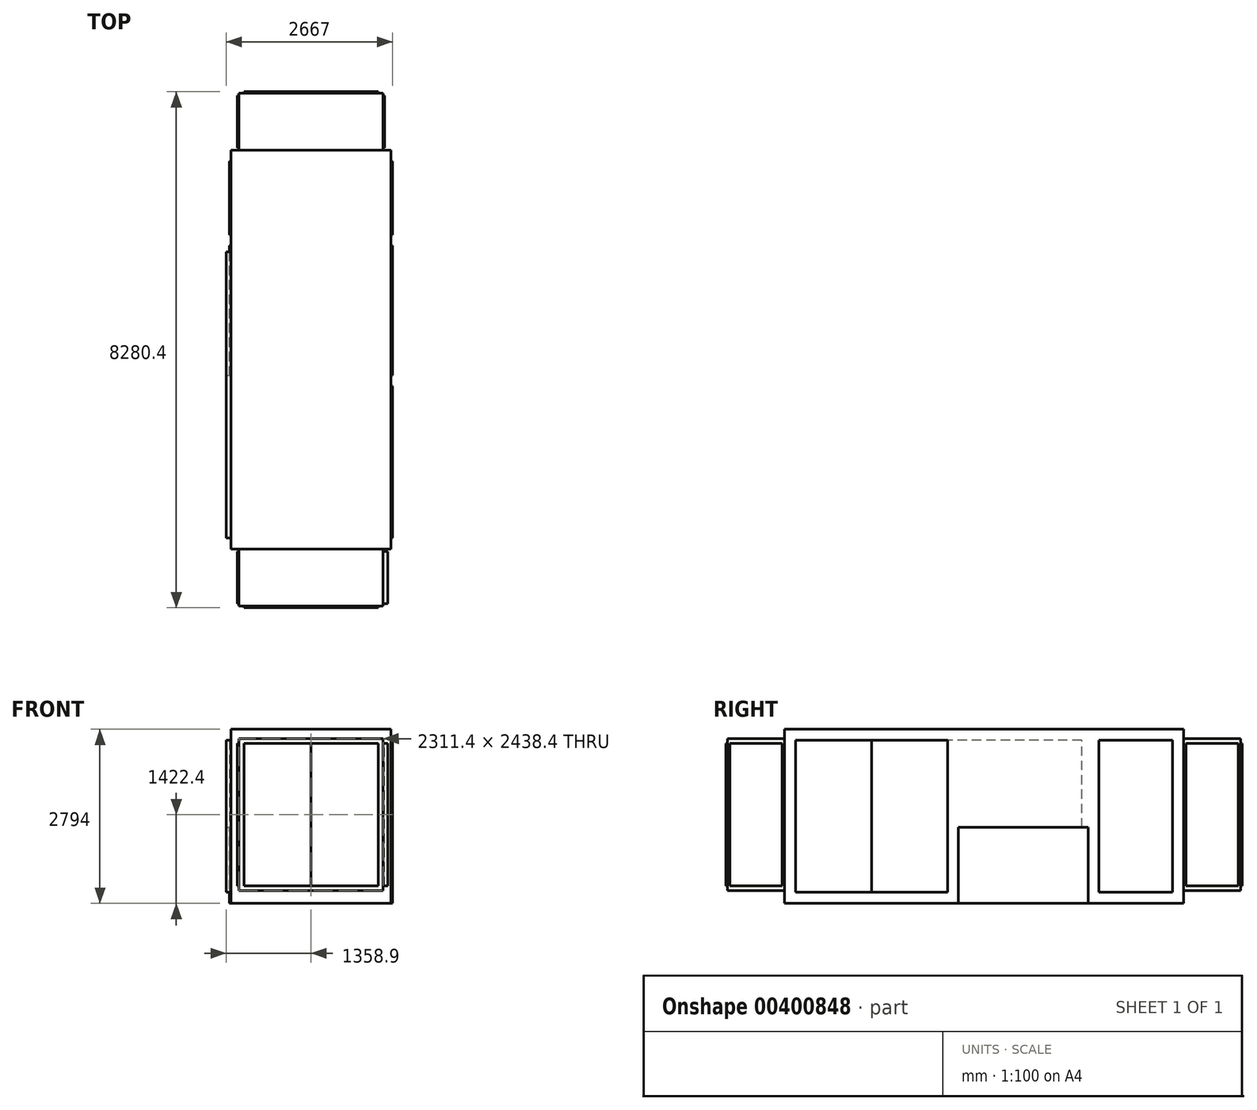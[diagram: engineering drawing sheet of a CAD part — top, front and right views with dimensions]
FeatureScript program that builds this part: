
annotation { "Feature Type Name" : "Feature", "Feature Type Description" : "" }
export const myFeature = defineFeature(function(context is Context, id is Id, definition is map)
    precondition{}
    {
        {
            var Q0;
            Q0=qCreatedBy(makeId("Top.planeOp"),FACE);
            var sketch = newSketch(context, id + "F0", { "sketchPlane" : qUnion([Q0])});
            skLineSegment(sketch, "E0.bottom", {"start": v(0, 0) * mm, "end": v(2565.4, 0) * mm});
            skLineSegment(sketch, "E0.top", {"start": v(0, 6400.8) * mm, "end": v(2565.4, 6400.8) * mm});
            skLineSegment(sketch, "E0.left", {"start": v(0, 0) * mm, "end": v(0, 6400.8) * mm});
            skLineSegment(sketch, "E0.right", {"start": v(2565.4, 0) * mm, "end": v(2565.4, 6400.8) * mm});
            skSolve(sketch);
        }
        {
            var Q0;
            Q0=qSketchRegion(id+"F0",true);
            extrude(context, id + "F1", {"entities" : qUnion([Q0]), "depth" : 2794 * mm});
        }
        {
            var Q0;
            Q0=makeQuery(id+"F1.opExtrude","SWEPT_FACE",FACE,{"disambiguationData":[OSD([sQuery(id+"F0.wireOp",EDGE,"E0.bottom")])]});
            var sketch = newSketch(context, id + "F2", { "sketchPlane" : qUnion([Q0])});
            skLineSegment(sketch, "E1.bottom", {"start": v(127, 203.2) * mm, "end": v(2438.4, 203.2) * mm});
            skLineSegment(sketch, "E1.top", {"start": v(127, 2641.6) * mm, "end": v(2438.4, 2641.6) * mm});
            skLineSegment(sketch, "E1.left", {"start": v(127, 203.2) * mm, "end": v(127, 2641.6) * mm});
            skLineSegment(sketch, "E1.right", {"start": v(2438.4, 203.2) * mm, "end": v(2438.4, 2641.6) * mm});
            skSolve(sketch);
        }
        {
            var Q0;
            Q0=qSketchRegion(id+"F2",true);
            extrude(context, id + "F3", {"entities" : qUnion([Q0]), "operationType" : NewBodyOperationType.ADD, "depth" : 914.4 * mm, "hasSecondDirection" : true, "secondDirectionOppositeDirection" : true, "secondDirectionDepth" : 7315.2 * mm});
        }
        {
            var Q0;
            Q0=makeQuery(id+"F3.opExtrude","CAP_FACE",FACE,{"disambiguationData":[OSD([sQuery(id+"F2.wireOp",EDGE,"E1.bottom"),sQuery(id+"F2.wireOp",EDGE,"E1.top"),sQuery(id+"F2.wireOp",EDGE,"E1.left"),sQuery(id+"F2.wireOp",EDGE,"E1.right")])],"isStart":false});
            var sketch = newSketch(context, id + "F4", { "sketchPlane" : qUnion([Q0])});
            skLineSegment(sketch, "E2.bottom", {"start": v(206.38, 279.4) * mm, "end": v(1282.7, 279.4) * mm});
            skLineSegment(sketch, "E2.top", {"start": v(206.38, 2565.4) * mm, "end": v(1282.7, 2565.4) * mm});
            skLineSegment(sketch, "E2.left", {"start": v(206.38, 279.4) * mm, "end": v(206.38, 2565.4) * mm});
            skLineSegment(sketch, "E2.right", {"start": v(1282.7, 279.4) * mm, "end": v(1282.7, 2565.4) * mm});
            skLineSegment(sketch, "E3.bottom", {"start": v(2359.03, 279.4) * mm, "end": v(1282.7, 279.4) * mm});
            skLineSegment(sketch, "E3.top", {"start": v(2359.03, 2565.4) * mm, "end": v(1282.7, 2565.4) * mm});
            skLineSegment(sketch, "E3.left", {"start": v(2359.03, 279.4) * mm, "end": v(2359.03, 2565.4) * mm});
            skPoint(sketch, "E4", {"position": v(1282.7, 203.2) * mm});
            skPoint(sketch, "E5", {"position": v(2359.03, 1422.4) * mm});
            skPoint(sketch, "E6", {"position": v(2438.4, 1422.4) * mm});
            skSolve(sketch);
        }
        {
            var Q0;
            Q0=makeQuery(id+"F3.opExtrude","CAP_FACE",FACE,{"disambiguationData":[OSD([sQuery(id+"F2.wireOp",EDGE,"E1.bottom"),sQuery(id+"F2.wireOp",EDGE,"E1.top"),sQuery(id+"F2.wireOp",EDGE,"E1.left"),sQuery(id+"F2.wireOp",EDGE,"E1.right")])],"isStart":true});
            var sketch = newSketch(context, id + "F5", { "sketchPlane" : qUnion([Q0])});
            skLineSegment(sketch, "E7.bottom", {"start": v(-2359.02, 279.4) * mm, "end": v(-1282.7, 279.4) * mm});
            skLineSegment(sketch, "E7.top", {"start": v(-2359.02, 2565.4) * mm, "end": v(-1282.7, 2565.4) * mm});
            skLineSegment(sketch, "E7.left", {"start": v(-2359.02, 279.4) * mm, "end": v(-2359.02, 2565.4) * mm});
            skLineSegment(sketch, "E7.right", {"start": v(-1282.7, 279.4) * mm, "end": v(-1282.7, 2565.4) * mm});
            skLineSegment(sketch, "E8.bottom", {"start": v(-206.37, 279.4) * mm, "end": v(-1282.7, 279.4) * mm});
            skLineSegment(sketch, "E8.top", {"start": v(-206.37, 2565.4) * mm, "end": v(-1282.7, 2565.4) * mm});
            skLineSegment(sketch, "E8.left", {"start": v(-206.37, 279.4) * mm, "end": v(-206.37, 2565.4) * mm});
            skPoint(sketch, "E9", {"position": v(-1282.7, 203.2) * mm});
            skPoint(sketch, "E10", {"position": v(-206.37, 1422.4) * mm});
            skPoint(sketch, "E11", {"position": v(-127, 1422.4) * mm});
            skSolve(sketch);
        }
        {
            var Q0;
            Q0=makeQuery(id+"F1.opExtrude","SWEPT_FACE",FACE,{"disambiguationData":[OSD([sQuery(id+"F0.wireOp",EDGE,"E0.right")])]});
            var sketch = newSketch(context, id + "F6", { "sketchPlane" : qUnion([Q0])});
            skLineSegment(sketch, "E12.bottom", {"start": v(177.8, 177.8) * mm, "end": v(1397, 177.8) * mm});
            skLineSegment(sketch, "E12.top", {"start": v(177.8, 2616.2) * mm, "end": v(1397, 2616.2) * mm});
            skLineSegment(sketch, "E12.left", {"start": v(177.8, 177.8) * mm, "end": v(177.8, 2616.2) * mm});
            skLineSegment(sketch, "E12.right", {"start": v(1397, 177.8) * mm, "end": v(1397, 2616.2) * mm});
            skLineSegment(sketch, "E13.bottom", {"start": v(1397, 177.8) * mm, "end": v(2616.2, 177.8) * mm});
            skLineSegment(sketch, "E13.top", {"start": v(1397, 2616.2) * mm, "end": v(2616.2, 2616.2) * mm});
            skLineSegment(sketch, "E13.right", {"start": v(2616.2, 177.8) * mm, "end": v(2616.2, 2616.2) * mm});
            skLineSegment(sketch, "E14", {"start": v(0, 1397) * mm, "end": v(177.8, 1397) * mm, "construction": true});
            skLineSegment(sketch, "E15", {"start": v(1397, 2794) * mm, "end": v(1397, 2616.2) * mm, "construction": true});
            skLineSegment(sketch, "E16.bottom", {"start": v(6223, 2616.2) * mm, "end": v(5041.9, 2616.2) * mm});
            skLineSegment(sketch, "E16.top", {"start": v(6223, 177.8) * mm, "end": v(5041.9, 177.8) * mm});
            skLineSegment(sketch, "E16.left", {"start": v(6223, 2616.2) * mm, "end": v(6223, 177.8) * mm});
            skLineSegment(sketch, "E16.right", {"start": v(5041.9, 2616.2) * mm, "end": v(5041.9, 177.8) * mm});
            skLineSegment(sketch, "E17", {"start": v(6223, 1397) * mm, "end": v(6400.8, 1397) * mm, "construction": true});
            skLineSegment(sketch, "E18.bottom", {"start": v(2787.65, 0) * mm, "end": v(4870.45, 0) * mm});
            skLineSegment(sketch, "E18.top", {"start": v(2787.65, 1219.2) * mm, "end": v(4870.45, 1219.2) * mm});
            skLineSegment(sketch, "E18.left", {"start": v(2787.65, 0) * mm, "end": v(2787.65, 1219.2) * mm});
            skLineSegment(sketch, "E18.right", {"start": v(4870.45, 0) * mm, "end": v(4870.45, 1219.2) * mm});
            skPoint(sketch, "E19", {"position": v(3829.05, 1219.2) * mm});
            skLineSegment(sketch, "E20.bottom", {"start": v(2889.25, 1219.2) * mm, "end": v(4768.85, 1219.2) * mm});
            skLineSegment(sketch, "E20.top", {"start": v(2889.25, 2616.2) * mm, "end": v(4768.85, 2616.2) * mm});
            skLineSegment(sketch, "E20.left", {"start": v(2889.25, 1219.2) * mm, "end": v(2889.25, 2616.2) * mm});
            skLineSegment(sketch, "E20.right", {"start": v(4768.85, 1219.2) * mm, "end": v(4768.85, 2616.2) * mm});
            skLineSegment(sketch, "E21", {"start": v(2616.2, 177.8) * mm, "end": v(2787.65, 177.8) * mm, "construction": true});
            skLineSegment(sketch, "E22", {"start": v(5041.9, 177.8) * mm, "end": v(4870.45, 177.8) * mm, "construction": true});
            skSolve(sketch);
        }
        {
            var Q0;
            Q0=makeQuery(id+"F1.opExtrude","SWEPT_FACE",FACE,{"disambiguationData":[OSD([sQuery(id+"F0.wireOp",EDGE,"E0.left")])]});
            var sketch = newSketch(context, id + "F7", { "sketchPlane" : qUnion([Q0])});
            skLineSegment(sketch, "E23.0.0", {"start": v(-5041.9, 177.8) * mm, "end": v(-6223, 177.8) * mm});
            skLineSegment(sketch, "E23.0.1", {"start": v(-6223, 177.8) * mm, "end": v(-6223, 2616.2) * mm});
            skLineSegment(sketch, "E23.0.2", {"start": v(-6223, 2616.2) * mm, "end": v(-5041.9, 2616.2) * mm});
            skLineSegment(sketch, "E23.0.3", {"start": v(-5041.9, 2616.2) * mm, "end": v(-5041.9, 177.8) * mm});
            skLineSegment(sketch, "E23.1.0", {"start": v(-2787.65, 1219.2) * mm, "end": v(-2787.65, 0) * mm});
            skLineSegment(sketch, "E23.1.1", {"start": v(-2787.65, 0) * mm, "end": v(-4870.45, 0) * mm});
            skLineSegment(sketch, "E23.1.2", {"start": v(-4870.45, 0) * mm, "end": v(-4870.45, 1219.2) * mm});
            skLineSegment(sketch, "E24", {"start": v(-4870.45, 1219.2) * mm, "end": v(-2787.65, 1219.2) * mm});
            skSolve(sketch);
        }
        {
            var Q0;
            {var subQ1=sQuery(id+"F2.wireOp",EDGE,"E1.left");Q0=makeQuery(id+"F3.boolean.opBoolean","SPLIT",FACE,{"disambiguationData":[TD([makeQuery(id+"F1.opExtrude","SWEPT_FACE",FACE,{"disambiguationData":[OSD([sQuery(id+"F0.wireOp",EDGE,"E0.top")])]})])],"derivedFrom":makeQuery(id+"F3.opExtrude","SWEPT_FACE",FACE,{"disambiguationData":[OSD([subQ1])]})});}
            var sketch = newSketch(context, id + "F8", { "sketchPlane" : qUnion([Q0])});
            skLineSegment(sketch, "E25.bottom", {"start": v(-7277.1, 279.4) * mm, "end": v(-6438.9, 279.4) * mm});
            skLineSegment(sketch, "E25.top", {"start": v(-7277.1, 2565.4) * mm, "end": v(-6438.9, 2565.4) * mm});
            skLineSegment(sketch, "E25.left", {"start": v(-7277.1, 279.4) * mm, "end": v(-7277.1, 2565.4) * mm});
            skLineSegment(sketch, "E25.right", {"start": v(-6438.9, 279.4) * mm, "end": v(-6438.9, 2565.4) * mm});
            skPoint(sketch, "E26", {"position": v(-6438.9, 1422.4) * mm});
            skPoint(sketch, "E27", {"position": v(-6858, 279.4) * mm});
            skSolve(sketch);
        }
        {
            var Q0;
            {var subQ0=sQuery(id+"F2.wireOp",EDGE,"E1.left");Q0=makeQuery(id+"F3.boolean.opBoolean","SPLIT",FACE,{"disambiguationData":[TD([makeQuery(id+"F1.opExtrude","SWEPT_FACE",FACE,{"disambiguationData":[OSD([sQuery(id+"F0.wireOp",EDGE,"E0.bottom")])]})])],"derivedFrom":makeQuery(id+"F3.opExtrude","SWEPT_FACE",FACE,{"disambiguationData":[OSD([subQ0])]})});}
            var sketch = newSketch(context, id + "F9", { "sketchPlane" : qUnion([Q0])});
            skLineSegment(sketch, "E28.bottom", {"start": v(38.1, 279.4) * mm, "end": v(876.3, 279.4) * mm});
            skLineSegment(sketch, "E28.top", {"start": v(38.1, 2565.4) * mm, "end": v(876.3, 2565.4) * mm});
            skLineSegment(sketch, "E28.left", {"start": v(38.1, 279.4) * mm, "end": v(38.1, 2565.4) * mm});
            skLineSegment(sketch, "E28.right", {"start": v(876.3, 279.4) * mm, "end": v(876.3, 2565.4) * mm});
            skPoint(sketch, "E29", {"position": v(876.3, 1422.4) * mm});
            skPoint(sketch, "E30", {"position": v(457.2, 279.4) * mm});
            skSolve(sketch);
        }
        {
            var Q0;
            {var subQ1=sQuery(id+"F2.wireOp",EDGE,"E1.right");Q0=makeQuery(id+"F3.boolean.opBoolean","SPLIT",FACE,{"disambiguationData":[TD([makeQuery(id+"F1.opExtrude","SWEPT_FACE",FACE,{"disambiguationData":[OSD([sQuery(id+"F0.wireOp",EDGE,"E0.top")])]})])],"derivedFrom":makeQuery(id+"F3.opExtrude","SWEPT_FACE",FACE,{"disambiguationData":[OSD([subQ1])]})});}
            var sketch = newSketch(context, id + "F10", { "sketchPlane" : qUnion([Q0])});
            skLineSegment(sketch, "E31.0.0", {"start": v(6438.9, 2565.4) * mm, "end": v(7277.1, 2565.4) * mm});
            skLineSegment(sketch, "E31.0.1", {"start": v(7277.1, 2565.4) * mm, "end": v(7277.1, 279.4) * mm});
            skLineSegment(sketch, "E31.0.2", {"start": v(7277.1, 279.4) * mm, "end": v(6438.9, 279.4) * mm});
            skLineSegment(sketch, "E31.0.3", {"start": v(6438.9, 279.4) * mm, "end": v(6438.9, 2565.4) * mm});
            skSolve(sketch);
        }
        {
            var Q0;
            Q0=makeQuery(id+"F7.imprint","IMPRINT",FACE,{"disambiguationData":[TD([[makeQuery(id+"F7.imprint","IMPRINT",EDGE,{"derivedFrom":sQuery(id+"F7.wireOp",EDGE,"E23.0.0")}),1.0]])]});
            var sketch = newSketch(context, id + "F11", { "sketchPlane" : qUnion([Q0])});
            skLineSegment(sketch, "E32.bottom", {"start": v(-4768.85, 1219.2) * mm, "end": v(-2787.65, 1219.2) * mm});
            skLineSegment(sketch, "E32.top", {"start": v(-4768.85, 2616.2) * mm, "end": v(-177.8, 2616.2) * mm});
            skLineSegment(sketch, "E32.left", {"start": v(-4768.85, 1219.2) * mm, "end": v(-4768.85, 2616.2) * mm});
            skLineSegment(sketch, "E32.right", {"start": v(-177.8, 177.8) * mm, "end": v(-177.8, 2616.2) * mm});
            skLineSegment(sketch, "E33.top", {"start": v(-2787.65, 177.8) * mm, "end": v(-177.8, 177.8) * mm});
            skLineSegment(sketch, "E33.left", {"start": v(-2787.65, 1219.2) * mm, "end": v(-2787.65, 177.8) * mm});
            skSolve(sketch);
        }
        {
            var Q0;
            {var subQ0=sQuery(id+"F2.wireOp",EDGE,"E1.right");Q0=makeQuery(id+"F3.boolean.opBoolean","SPLIT",FACE,{"disambiguationData":[TD([makeQuery(id+"F1.opExtrude","SWEPT_FACE",FACE,{"disambiguationData":[OSD([sQuery(id+"F0.wireOp",EDGE,"E0.bottom")])]})])],"derivedFrom":makeQuery(id+"F3.opExtrude","SWEPT_FACE",FACE,{"disambiguationData":[OSD([subQ0])]})});}
            var sketch = newSketch(context, id + "F12", { "sketchPlane" : qUnion([Q0])});
            skLineSegment(sketch, "E34.0.0", {"start": v(-876.3, 2565.4) * mm, "end": v(-38.1, 2565.4) * mm});
            skLineSegment(sketch, "E34.0.1", {"start": v(-38.1, 2565.4) * mm, "end": v(-38.1, 279.4) * mm});
            skLineSegment(sketch, "E34.0.2", {"start": v(-38.1, 279.4) * mm, "end": v(-876.3, 279.4) * mm});
            skLineSegment(sketch, "E34.0.3", {"start": v(-876.3, 279.4) * mm, "end": v(-876.3, 2565.4) * mm});
            skSolve(sketch);
        }
        {
            var Q0;
            Q0=makeQuery(id+"F8.imprint","IMPRINT",FACE,{"disambiguationData":[TD([[makeQuery(id+"F8.imprint","IMPRINT",EDGE,{"derivedFrom":sQuery(id+"F8.wireOp",EDGE,"E25.bottom")}),1.0]])]});
            var Q1;
            Q1=makeQuery(id+"F7.imprint","IMPRINT",FACE,{"disambiguationData":[TD([[makeQuery(id+"F7.imprint","IMPRINT",EDGE,{"derivedFrom":sQuery(id+"F7.wireOp",EDGE,"E23.0.0")}),-1.0]])]});
            var Q2;
            Q2=makeQuery(id+"F7.imprint","IMPRINT",FACE,{"disambiguationData":[TD([[makeQuery(id+"F7.imprint","IMPRINT",EDGE,{"derivedFrom":sQuery(id+"F7.wireOp",EDGE,"E23.1.0")}),-1.0]])]});
            extrude(context, id + "F13", {"entities" : qUnion([Q0, Q1, Q2]), "depth" : 25.4 * mm, "offsetDistance" : 25.4 * mm});
        }
        {
            var Q0;
            Q0=makeQuery(id+"F5.imprint","IMPRINT",FACE,{"disambiguationData":[TD([[makeQuery(id+"F5.imprint","IMPRINT",EDGE,{"derivedFrom":sQuery(id+"F5.wireOp",EDGE,"E8.bottom")}),-1.0]])]});
            extrude(context, id + "F14", {"entities" : qUnion([Q0]), "depth" : 25.4 * mm, "offsetDistance" : 25.4 * mm});
        }
        {
            var Q0;
            Q0=makeQuery(id+"F5.imprint","IMPRINT",FACE,{"disambiguationData":[TD([[makeQuery(id+"F5.imprint","IMPRINT",EDGE,{"derivedFrom":sQuery(id+"F5.wireOp",EDGE,"E7.bottom")}),1.0]])]});
            extrude(context, id + "F15", {"entities" : qUnion([Q0]), "depth" : 25.4 * mm, "offsetDistance" : 25.4 * mm});
        }
        {
            var Q0;
            Q0=makeQuery(id+"F6.imprint","IMPRINT",FACE,{"disambiguationData":[TD([[makeQuery(id+"F6.imprint","IMPRINT",EDGE,{"derivedFrom":sQuery(id+"F6.wireOp",EDGE,"E20.bottom")}),1.0]])]});
            var Q1;
            Q1=makeQuery(id+"F6.imprint","IMPRINT",FACE,{"disambiguationData":[TD([[makeQuery(id+"F6.imprint","IMPRINT",EDGE,{"derivedFrom":sQuery(id+"F6.wireOp",EDGE,"E13.bottom")}),1.0]])]});
            extrude(context, id + "F16", {"entities" : qUnion([Q0, Q1]), "depth" : 25.4 * mm, "offsetDistance" : 25.4 * mm});
        }
        {
            var Q0;
            Q0=makeQuery(id+"F10.imprint","IMPRINT",FACE,{"disambiguationData":[TD([[makeQuery(id+"F10.imprint","IMPRINT",EDGE,{"derivedFrom":sQuery(id+"F10.wireOp",EDGE,"E31.0.0")}),-1.0]])]});
            var Q1;
            Q1=makeQuery(id+"F6.imprint","IMPRINT",FACE,{"disambiguationData":[TD([[makeQuery(id+"F6.imprint","IMPRINT",EDGE,{"derivedFrom":sQuery(id+"F6.wireOp",EDGE,"E16.bottom")}),1.0]])]});
            var Q2;
            Q2=makeQuery(id+"F6.imprint","IMPRINT",FACE,{"disambiguationData":[TD([[makeQuery(id+"F6.imprint","IMPRINT",EDGE,{"derivedFrom":sQuery(id+"F6.wireOp",EDGE,"E18.bottom")}),1.0]])]});
            var Q3;
            Q3=makeQuery(id+"F6.imprint","IMPRINT",FACE,{"disambiguationData":[TD([[makeQuery(id+"F6.imprint","IMPRINT",EDGE,{"derivedFrom":sQuery(id+"F6.wireOp",EDGE,"E12.bottom")}),1.0]])]});
            extrude(context, id + "F17", {"entities" : qUnion([Q0, Q1, Q2, Q3]), "depth" : 25.4 * mm, "offsetDistance" : 25.4 * mm});
        }
        {
            var Q0;
            Q0=makeQuery(id+"F11.imprint","IMPRINT",FACE,{"disambiguationData":[TD([[makeQuery(id+"F11.imprint","IMPRINT",EDGE,{"derivedFrom":sQuery(id+"F11.wireOp",EDGE,"E32.bottom")}),1.0]])]});
            extrude(context, id + "F18", {"entities" : qUnion([Q0]), "depth" : 76.2 * mm, "offsetDistance" : 25.4 * mm});
        }
        {
            var Q0;
            Q0=makeQuery(id+"F12.imprint","IMPRINT",FACE,{"disambiguationData":[TD([[makeQuery(id+"F12.imprint","IMPRINT",EDGE,{"derivedFrom":sQuery(id+"F12.wireOp",EDGE,"E34.0.0")}),-1.0]])]});
            extrude(context, id + "F19", {"entities" : qUnion([Q0]), "depth" : 76.2 * mm, "offsetDistance" : 25.4 * mm});
        }
        {
            var Q0;
            Q0=makeQuery(id+"F4.imprint","IMPRINT",FACE,{"disambiguationData":[TD([[makeQuery(id+"F4.imprint","IMPRINT",EDGE,{"derivedFrom":sQuery(id+"F4.wireOp",EDGE,"E3.bottom")}),-1.0]])]});
            extrude(context, id + "F20", {"entities" : qUnion([Q0]), "depth" : 25.4 * mm, "offsetDistance" : 25.4 * mm});
        }
        {
            var Q0;
            Q0=makeQuery(id+"F4.imprint","IMPRINT",FACE,{"disambiguationData":[TD([[makeQuery(id+"F4.imprint","IMPRINT",EDGE,{"derivedFrom":sQuery(id+"F4.wireOp",EDGE,"E2.bottom")}),1.0]])]});
            extrude(context, id + "F21", {"entities" : qUnion([Q0]), "depth" : 25.4 * mm, "offsetDistance" : 25.4 * mm});
        }
        {
            var Q0;
            Q0=makeQuery(id+"F9.imprint","IMPRINT",FACE,{"disambiguationData":[TD([[makeQuery(id+"F9.imprint","IMPRINT",EDGE,{"derivedFrom":sQuery(id+"F9.wireOp",EDGE,"E28.bottom")}),1.0]])]});
            extrude(context, id + "F22", {"entities" : qUnion([Q0]), "depth" : 25.4 * mm, "offsetDistance" : 25.4 * mm});
        }
    });
